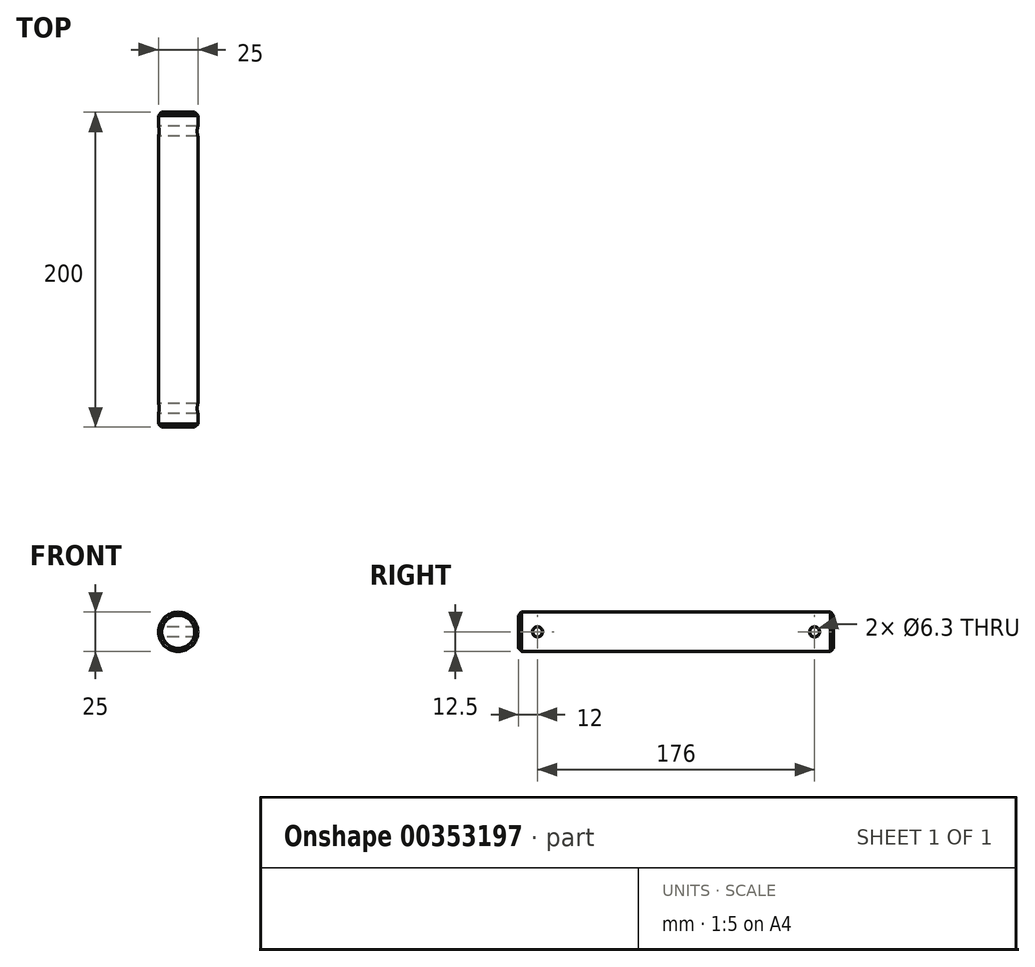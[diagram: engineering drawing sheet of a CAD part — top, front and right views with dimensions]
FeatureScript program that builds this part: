
annotation { "Feature Type Name" : "Feature", "Feature Type Description" : "" }
export const myFeature = defineFeature(function(context is Context, id is Id, definition is map)
    precondition{}
    {
        {
            var Q0;
            Q0=qCreatedBy(makeId("Front.planeOp"),FACE);
            var sketch = newSketch(context, id + "F0", { "sketchPlane" : qUnion([Q0])});
            skCircle(sketch, "E0", {"center": v(0, 0) * mm, "radius": 12.5 * mm});
            skSolve(sketch);
        }
        {
            var Q0;
            Q0 = qSketchRegion(id + "F0", true);
            extrude(context, id + "F1", {"entities" : qUnion([Q0]), "depth" : 200 * mm});
        }
        {
            var Q0;
            Q0=qCreatedBy(makeId("Right.planeOp"),FACE);
            var sketch = newSketch(context, id + "F2", { "sketchPlane" : qUnion([Q0])});
            skLineSegment(sketch, "E1", {"start": v(0, -12.5) * mm, "end": v(-200, -12.5) * mm});
            skLineSegment(sketch, "E2", {"start": v(-200, 12.5) * mm, "end": v(0, 12.5) * mm});
            skCircle(sketch, "E3", {"center": v(-12, 0) * mm, "radius": 3.15 * mm});
            skCircle(sketch, "E4", {"center": v(-188, 0) * mm, "radius": 3.15 * mm});
            skSolve(sketch);
        }
        {
            var Q0;
            Q0 = qSketchRegion(id + "F2", true);
            extrude(context, id + "F3", {"entities" : qUnion([Q0]), "operationType" : NewBodyOperationType.REMOVE, "endBound" : BoundingType.SYMMETRIC, "depth" : 130 * mm});
        }
        {
            var Q0;
            Q0=makeQuery(id+"F1.opExtrude","CAP_EDGE",EDGE,{"disambiguationData":[OSD([sQuery(id+"F0.wireOp",EDGE,"E0")])],"isStart":true});
            var Q1;
            Q1=makeQuery(id+"F1.opExtrude","CAP_EDGE",EDGE,{"disambiguationData":[OSD([sQuery(id+"F0.wireOp",EDGE,"E0")])],"isStart":false});
            chamfer(context, id + "F4", {"entities" : qUnion([Q0, Q1]), "width" : 2 * mm, "tangentPropagation" : true});
        }
    });
